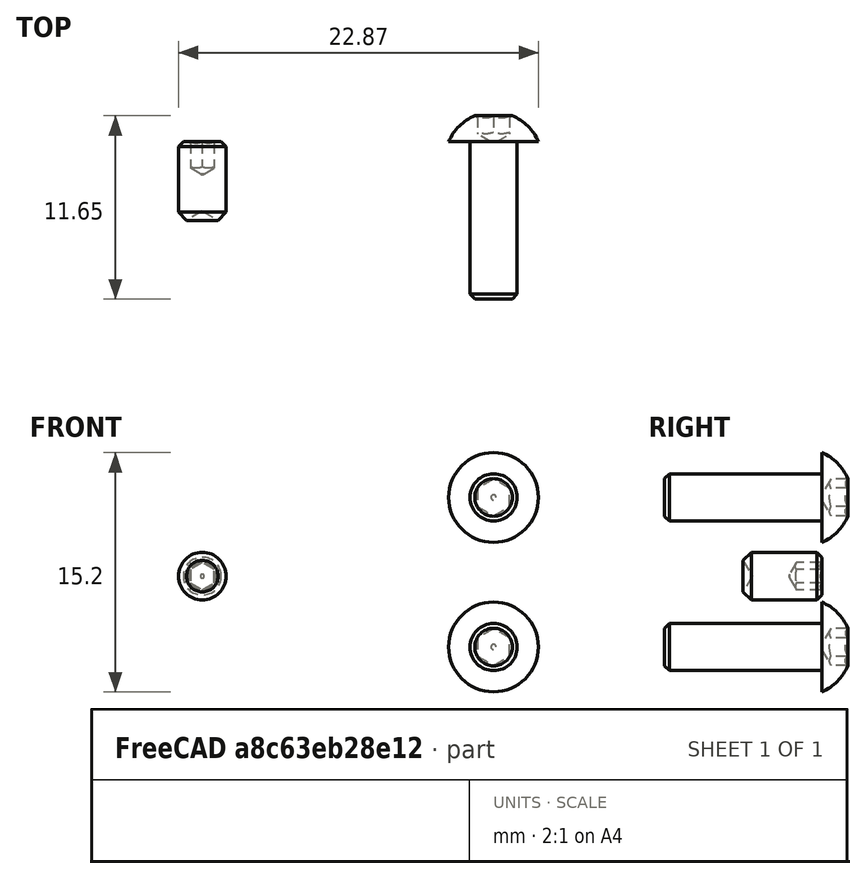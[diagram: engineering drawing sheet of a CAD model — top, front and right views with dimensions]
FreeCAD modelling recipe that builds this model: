
FCSTD DOCUMENT  (FreeCAD 0.19R24267 (Git))
Label: e3d_volcano_assembly
License: All rights reserved
LicenseURL: http://en.wikipedia.org/wiki/All_rights_reserved
objects: App::Link×4, Part::FeaturePython×3, App::DocumentObjectGroup×2, PartDesign::CoordinateSystem×1, App::FeaturePython×1, App::Part×1
note: 4 computed .brp shape members not serialized (recipe doc carries the construction recipe); baked Part::Feature solids carry a one-line shape summary decoded from their .brp
EXTERNAL_REF file=volcano_heat_break.FCStd obj=LCS_1
EXTERNAL_REF file=volcano_heat_break.FCStd obj=Part
EXTERNAL_REF file=volcano_heat_break.FCStd obj=LCS_3
EXTERNAL_REF file=volcano_nozzle.FCStd obj=LCS_1
EXTERNAL_REF file=volcano_nozzle.FCStd obj=Part
EXTERNAL_REF file=Volcano_Heater_Block.FCStd obj=LCS_1
EXTERNAL_REF file=volcano_heat_break.FCStd obj=LCS_2
EXTERNAL_REF file=Volcano_Heater_Block.FCStd obj=Part
EXTERNAL_REF file=Volcano_Heater_Block.FCStd obj=LCS_3
EXTERNAL_REF file=heater_cartridge.FCStd obj=LCS_1
EXTERNAL_REF file=heater_cartridge.FCStd obj=Part049
EXTERNAL_REF file=Volcano_Heater_Block.FCStd obj=LCS_4
EXTERNAL_REF file=Volcano_Heater_Block.FCStd obj=LCS_5
EXTERNAL_REF file=Volcano_Heater_Block.FCStd obj=LCS_6

FEATURE [App::DocumentObjectGroup] Parts
FEATURE [PartDesign::CoordinateSystem] LCS_Origin
  AttacherType = Attacher::AttachEngine3D
  MapMode = 2
  Support = -> [X_Axis]
FEATURE [App::DocumentObjectGroup] Constraints
FEATURE [App::FeaturePython] Variables  # WARN: FeaturePython — macro-defined, semantics opaque (R4)
FEATURE [App::Link] volcano_heat_break_volcano_heat_break
  AssemblyType = Asm4EE
  AttachedBy = #LCS_1
  AttachedTo = Parent Assembly#LCS_Origin
  AttachmentOffset = pos=(0,0,0) rot=(0,1,0;3.14159rad)
  LinkPlacement = pos=(50,-7.1e-15,-7.75) rot=(0,0,1;4.71239rad)
  LinkedObject = -> <external volcano_heat_break.FCStd>#Part
  Placement = pos=(50,-7.1e-15,-7.75) rot=(0,0,1;4.71239rad)
  expr: Placement = LCS_Origin.Placement * AttachmentOffset * volcano_heat_break#LCS_1.Placement ^ -1
FEATURE [App::Link] volcano_nozzle_volcano_nozzle
  AssemblyType = Asm4EE
  AttachedBy = #LCS_1
  AttachedTo = volcano_heat_break_volcano_heat_break#LCS_3
  AttachmentOffset = pos=(0,0,0) rot=(0,1,0;3.14159rad)
  LinkPlacement = pos=(2.2e-14,1.3e-15,-28.745) rot=(0,0,1;1.5708rad)
  LinkedObject = -> <external volcano_nozzle.FCStd>#Part
  Placement = pos=(2.2e-14,1.3e-15,-28.745) rot=(0,0,1;1.5708rad)
  expr: Placement = volcano_heat_break_volcano_heat_break.Placement * volcano_heat_break#LCS_3.Placement * AttachmentOffset * volcano_nozzle#LCS_1.Placement ^ -1
FEATURE [App::Link] Volcano_Heater_Block_Volcano_Heater_Block
  AssemblyType = Asm4EE
  AttachedBy = #LCS_1
  AttachedTo = volcano_heat_break_volcano_heat_break#LCS_2
  AttachmentOffset = pos=(0,0,0) rot=(0,0,1;3.14159rad)
  LinkPlacement = pos=(15.5,-7,-22.5) rot=(0,-0.707107,-0.707107;3.14159rad)
  LinkedObject = -> <external Volcano_Heater_Block.FCStd>#Part
  Placement = pos=(15.5,-7,-22.5) rot=(0,-0.707107,-0.707107;3.14159rad)
  expr: Placement = volcano_heat_break_volcano_heat_break.Placement * volcano_heat_break#LCS_2.Placement * AttachmentOffset * Volcano_Heater_Block#LCS_1.Placement ^ -1
FEATURE [App::Link] heater_cartridge_heater_cartridge
  AssemblyType = Asm4EE
  AttachedBy = #LCS_1
  AttachedTo = Volcano_Heater_Block_Volcano_Heater_Block#LCS_3
  LinkPlacement = pos=(7.5,0.5,-2.5) rot=(0,0,1;6.28279rad)
  LinkedObject = -> <external heater_cartridge.FCStd>#Part049
  Placement = pos=(7.5,0.5,-2.5) rot=(0,0,1;6.28279rad)
  expr: Placement = Volcano_Heater_Block_Volcano_Heater_Block.Placement * Volcano_Heater_Block#LCS_3.Placement * AttachmentOffset * heater_cartridge#LCS_1.Placement ^ -1
FEATURE [Part::FeaturePython] Screw  label="M3x10-Screw"  # Fasteners workbench fastener (typed FeaturePython)
  AssemblyType = Asm4EE
  AttachedBy = Origin
  AttachedTo = Volcano_Heater_Block_Volcano_Heater_Block#LCS_4
  Placement = pos=(13,4.5,-7.5) rot=(-0.57735,-0.57735,-0.57735;2.0944rad)
  diameter = 1
  invert = false
  length = 2
  lengthCustom = 10
  matchOuter = false
  offset = 0
  thread = false
  type = 38
  expr: Placement = Volcano_Heater_Block_Volcano_Heater_Block.Placement * Volcano_Heater_Block#LCS_4.Placement * AttachmentOffset
FEATURE [Part::FeaturePython] Screw001  label="M3x10-Screw001"  # Fasteners workbench fastener (typed FeaturePython)
  AssemblyType = Asm4EE
  AttachedBy = Origin
  AttachedTo = Volcano_Heater_Block_Volcano_Heater_Block#LCS_5
  Placement = pos=(13,4.5,-17) rot=(-0.57735,-0.57735,-0.57735;2.0944rad)
  diameter = 1
  invert = false
  length = 2
  lengthCustom = 10
  matchOuter = false
  offset = 0
  thread = false
  type = 38
  expr: Placement = Volcano_Heater_Block_Volcano_Heater_Block.Placement * Volcano_Heater_Block#LCS_5.Placement * AttachmentOffset
FEATURE [Part::FeaturePython] Screw002  label="M3x5-Screw"  # Fasteners workbench fastener (typed FeaturePython)
  AssemblyType = Asm4EE
  AttachedBy = Origin
  AttachedTo = Volcano_Heater_Block_Volcano_Heater_Block#LCS_6
  Placement = pos=(-5.5,4.5,-12.5) rot=(-0.57735,-0.57735,-0.57735;2.0944rad)
  diameter = 6
  invert = false
  length = 3
  lengthCustom = 5
  matchOuter = false
  offset = 0
  thread = false
  type = 31
  expr: Placement = Volcano_Heater_Block_Volcano_Heater_Block.Placement * Volcano_Heater_Block#LCS_6.Placement * AttachmentOffset
FEATURE [App::Part] Model
  Configuration = 0
  Group = -> [LCS_Origin,Constraints,Variables,volcano_heat_break_volcano_heat_break,volcano_nozzle_volcano_nozzle,Volcano_Heater_Block_Volcano_Heater_Block,heater_cartridge_heater_cartridge,Screw,Screw001,Screw002]
  Origin = -> Origin
  Type = Assembly4 Model

RESOLVED EXTERNAL PARTS (link-assembly join: the EXTERNAL_REF files above that resolve inside this repo's crawl, each included once):
---- part heater_cartridge.FCStd = doc fcstd_1dd9fb010104 ----
FCSTD DOCUMENT  (FreeCAD 0.19R24267 (Git))
Label: heater_cartridge
License: All rights reserved
LicenseURL: http://en.wikipedia.org/wiki/All_rights_reserved
objects: Sketcher::SketchObject×5, PartDesign::Body×3, PartDesign::AdditivePipe×2, PartDesign::Pad×1, PartDesign::Boolean×1, PartDesign::CoordinateSystem×1, App::Part×1
note: 16 computed .brp shape members not serialized (recipe doc carries the construction recipe); baked Part::Feature solids carry a one-line shape summary decoded from their .brp

FEATURE [Sketcher::SketchObject] Sketch087
  FullyConstrained = false
  MapMode = 5
  Placement = pos=(0,0,0) rot=(1,0,0;1.5708rad)
  Support = -> [XZ_Plane101]
  sketch-geometry (5):
    g0: ArcOfCircle CenterX=1.32205 CenterY=0 CenterZ=0 NormalX=0 NormalY=0 NormalZ=1 AngleXU=0 Radius=1.32205 StartAngle=1.5708 EndAngle=3.14159
    g1: LineSegment StartX=1.32205 StartY=1.32205 StartZ=0 EndX=16.6441 EndY=1.32205 EndZ=0
    g2: ArcOfCircle CenterX=16.6441 CenterY=12.6746 CenterZ=0 NormalX=0 NormalY=0 NormalZ=1 AngleXU=0 Radius=11.3525 StartAngle=4.71239 EndAngle=7.33941
    g3: ArcOfCircle CenterX=31.8557 CenterY=39.5797 CenterZ=0 NormalX=0 NormalY=0 NormalZ=1 AngleXU=0 Radius=19.555 StartAngle=3.14159 EndAngle=4.19782
    g4: LineSegment StartX=12.3007 StartY=39.5797 StartZ=0 EndX=12.3007 EndY=66.5454 EndZ=0
  constraints (8):
    c: PointOnObject(g0,g-1)
    c: Coincident(g0,g-1)
    c: Horizontal(g1)
    c: Vertical(g4)
    c: Tangent(g3,g2) = 1.5708
    c: Tangent(g2,g1) = -1.5708
    c: Tangent(g1,g0) = 1.5708
    c: Tangent(g4,g3) = 1.5708
FEATURE [Sketcher::SketchObject] Sketch088
  FullyConstrained = false
  MapMode = 5
  Support = -> [XY_Plane101]
  sketch-geometry (1):
    g0: Circle CenterX=0 CenterY=0 CenterZ=0 NormalX=0 NormalY=0 NormalZ=1 AngleXU=0 Radius=1
  constraints (2):
    c: Coincident(g0,g-1)
    c: Diameter(g0) = 2
FEATURE [PartDesign::AdditivePipe] AdditivePipe003
  AuxilleryCurvelinear = true
  AuxillerySpineTangent = false
  Binormal = (0,0,0)
  Mode = 2
  Profile = -> Sketch088
  Spine = -> Sketch087
  SpineTangent = false
  Transformation = 0
  Transition = 0
FEATURE [PartDesign::Body] Body033  label="Body034"
  Group = -> [Sketch087,Sketch088,AdditivePipe003]
  Origin = -> Origin101
  Placement = pos=(0,0.99,0) rot=(0,0,1;0rad)
  Tip = -> AdditivePipe003
FEATURE [Sketcher::SketchObject] Sketch089
  FullyConstrained = false
  MapMode = 5
  Support = -> [XY_Plane102]
  sketch-geometry (1):
    g0: Circle CenterX=0 CenterY=0 CenterZ=0 NormalX=0 NormalY=0 NormalZ=1 AngleXU=0 Radius=1
  constraints (2):
    c: Coincident(g0,g-1)
    c: Diameter(g0) = 2
FEATURE [Sketcher::SketchObject] Sketch090
  FullyConstrained = false
  MapMode = 5
  Placement = pos=(0,0,0) rot=(1,0,0;1.5708rad)
  Support = -> [XZ_Plane102]
  sketch-geometry (5):
    g0: ArcOfCircle CenterX=1.32205 CenterY=0 CenterZ=0 NormalX=0 NormalY=0 NormalZ=1 AngleXU=0 Radius=1.32205 StartAngle=1.5708 EndAngle=3.14159
    g1: LineSegment StartX=1.32205 StartY=1.32205 StartZ=0 EndX=16.6441 EndY=1.32205 EndZ=0
    g2: ArcOfCircle CenterX=16.6441 CenterY=12.6746 CenterZ=0 NormalX=0 NormalY=0 NormalZ=1 AngleXU=0 Radius=11.3525 StartAngle=4.71239 EndAngle=7.33941
    g3: ArcOfCircle CenterX=31.8557 CenterY=39.5797 CenterZ=0 NormalX=0 NormalY=0 NormalZ=1 AngleXU=0 Radius=19.555 StartAngle=3.14159 EndAngle=4.19782
    g4: LineSegment StartX=12.3007 StartY=39.5797 StartZ=0 EndX=12.3007 EndY=66.5454 EndZ=0
  constraints (8):
    c: PointOnObject(g0,g-1)
    c: Coincident(g0,g-1)
    c: Horizontal(g1)
    c: Vertical(g4)
    c: Tangent(g3,g2) = 1.5708
    c: Tangent(g2,g1) = -1.5708
    c: Tangent(g1,g0) = 1.5708
    c: Tangent(g4,g3) = 1.5708
FEATURE [PartDesign::AdditivePipe] AdditivePipe004
  AuxilleryCurvelinear = true
  AuxillerySpineTangent = false
  Binormal = (0,0,0)
  Mode = 2
  Profile = -> Sketch089
  Spine = -> Sketch090
  SpineTangent = false
  Transformation = 0
  Transition = 0
FEATURE [PartDesign::Body] Body034  label="Body035"
  Group = -> [Sketch090,Sketch089,AdditivePipe004]
  Origin = -> Origin102
  Placement = pos=(0,-1.02,0) rot=(0,0,1;0rad)
  Tip = -> AdditivePipe004
FEATURE [Sketcher::SketchObject] Sketch
  FullyConstrained = false
  MapMode = 5
  Support = -> [XY_Plane]
  sketch-geometry (1):
    g0: Circle CenterX=0 CenterY=0 CenterZ=0 NormalX=0 NormalY=0 NormalZ=1 AngleXU=0 Radius=3
  constraints (2):
    c: Coincident(g0,g-1)
    c: Diameter(g0) = 6
FEATURE [PartDesign::Pad] Pad
  Direction = (1,1,1)
  Length = 20
  Length2 = 100
  Profile = -> Sketch
  Reversed = true
  Type = 0
FEATURE [PartDesign::Boolean] Boolean
  BaseFeature = -> Pad
  Group = -> [Body033,Body034]
  Type = 0
FEATURE [PartDesign::Body] Body
  Group = -> [Sketch,Pad,Boolean]
  Origin = -> Origin
  Tip = -> Boolean
FEATURE [PartDesign::CoordinateSystem] LCS_1
  AttacherType = Attacher::AttachEngine3D
  MapMode = 11
  Placement = pos=(0,0,-20) rot=(0,0,1;1.5708rad)
  Support = -> [Boolean]
FEATURE [App::Part] Part049  label="heater_cartridge"
  Group = -> [Body,LCS_1]
  Origin = -> Origin100
